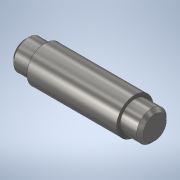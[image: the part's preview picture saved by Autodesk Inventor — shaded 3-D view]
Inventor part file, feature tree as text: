
AUTODESK INVENTOR PART (.ipt)
format: ipt  version: 2020 (Build 240168000, 168)  size: 123,392 bytes
history: native  units: mm
features: chamfer x2, revolve x1, sketch x1
ambient origin geometry x8: Origin, YZ Plane, XZ Plane, XY Plane, X Axis, Y Axis, Z Axis, Center Point
bodies: Solid1 (feature_tree)
feature tree (4):
  revolve  "Revolution1"  [1 undecoded]
  chamfer  "Chamfer1"  Distance=12.0mm
  chamfer  "Chamfer2"  Distance=2.0mm
  sketch  "Sketch1"  dims[d0=78.0mm d1=8.95mm d2=12.0mm d3=2.0mm d4=54.0mm d5=2.0mm d6=90.0deg d7=2.0mm d8=2.0mm d9=45.0deg d10=2.0mm d11=2.0mm d12=45.0deg]
note: 1 required parameter value undecoded (feature->parameter linkage not recoverable at this tier; creation-order binding heuristic only, values carry confidence <= 0.55)
